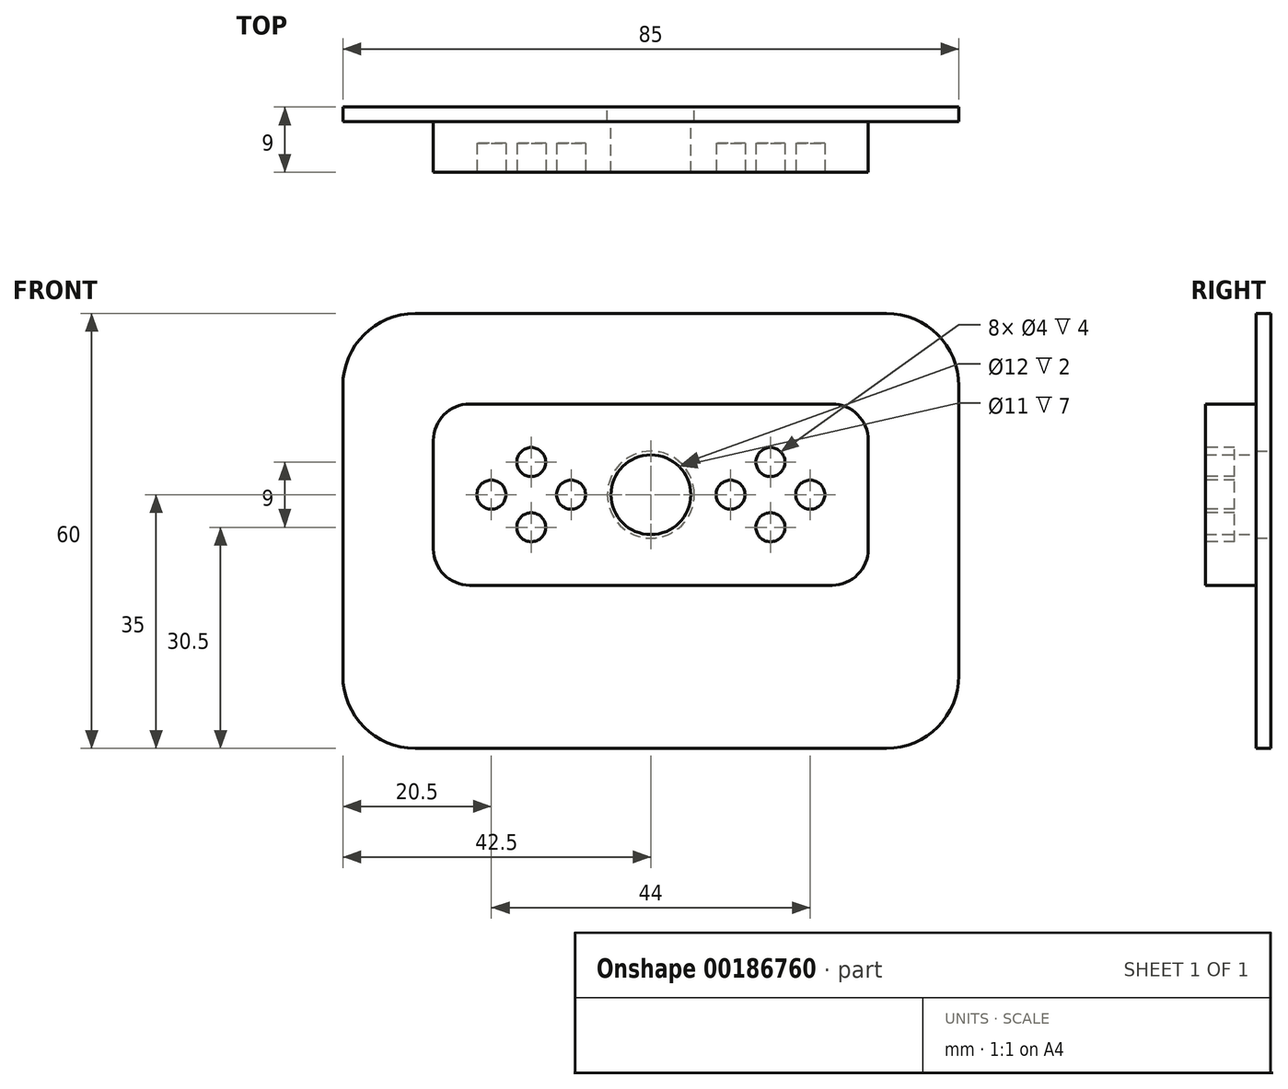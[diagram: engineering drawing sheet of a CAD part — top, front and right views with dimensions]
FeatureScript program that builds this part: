
annotation { "Feature Type Name" : "Feature", "Feature Type Description" : "" }
export const myFeature = defineFeature(function(context is Context, id is Id, definition is map)
    precondition{}
    {
        {
            var Q0;
            Q0=qCreatedBy(makeId("Front.planeOp"),FACE);
            var sketch = newSketch(context, id + "F0", { "sketchPlane" : qUnion([Q0])});
            skLineSegment(sketch, "E0.bottom", {"start": v(42.5, -35) * mm, "end": v(-42.5, -35) * mm});
            skLineSegment(sketch, "E0.top", {"start": v(42.5, 25) * mm, "end": v(-42.5, 25) * mm});
            skLineSegment(sketch, "E0.left", {"start": v(42.5, -35) * mm, "end": v(42.5, 25) * mm});
            skLineSegment(sketch, "E0.right", {"start": v(-42.5, -35) * mm, "end": v(-42.5, 25) * mm});
            skCircle(sketch, "E1", {"center": v(0, 0) * mm, "radius": 6 * mm});
            skSolve(sketch);
        }
        {
            var Q0;
            Q0 = qSketchRegion(id + "F0", true);
            extrude(context, id + "F1", {"entities" : qUnion([Q0]), "depth" : 2 * mm});
        }
        {
            var Q0;
            Q0=makeQuery(id+"F1.opExtrude","CAP_FACE",FACE,{"disambiguationData":[OSD([sQuery(id+"F0.wireOp",EDGE,"E0.bottom"),sQuery(id+"F0.wireOp",EDGE,"E0.top"),sQuery(id+"F0.wireOp",EDGE,"E0.left"),sQuery(id+"F0.wireOp",EDGE,"E0.right"),sQuery(id+"F0.wireOp",EDGE,"E1")])],"isStart":false});
            var sketch = newSketch(context, id + "F2", { "sketchPlane" : qUnion([Q0])});
            skLineSegment(sketch, "E2.bottom", {"start": v(-30, 12.5) * mm, "end": v(30, 12.5) * mm});
            skLineSegment(sketch, "E2.top", {"start": v(-30, -12.5) * mm, "end": v(30, -12.5) * mm});
            skLineSegment(sketch, "E2.left", {"start": v(-30, 12.5) * mm, "end": v(-30, -12.5) * mm});
            skLineSegment(sketch, "E2.right", {"start": v(30, 12.5) * mm, "end": v(30, -12.5) * mm});
            skPoint(sketch, "E2.middle", {"position": v(0, 0) * mm});
            skCircle(sketch, "E3", {"center": v(0, 0) * mm, "radius": 5.5 * mm});
            skSolve(sketch);
        }
        {
            var Q0;
            Q0 = qSketchRegion(id + "F2", true);
            extrude(context, id + "F3", {"entities" : qUnion([Q0]), "operationType" : NewBodyOperationType.ADD, "depth" : 7 * mm});
        }
        {
            var Q0;
            Q0=makeQuery(id+"F3.opExtrude","SWEPT_EDGE",EDGE,{"disambiguationData":[OSD([sQuery(id+"F2.wireOp",EDGE,"E2.bottom"),sQuery(id+"F2.wireOp",EDGE,"E2.right")])]});
            var Q1;
            Q1=makeQuery(id+"F3.opExtrude","SWEPT_EDGE",EDGE,{"disambiguationData":[OSD([sQuery(id+"F2.wireOp",EDGE,"E2.top"),sQuery(id+"F2.wireOp",EDGE,"E2.right")])]});
            var Q2;
            Q2=makeQuery(id+"F3.opExtrude","SWEPT_EDGE",EDGE,{"disambiguationData":[OSD([sQuery(id+"F2.wireOp",EDGE,"E2.top"),sQuery(id+"F2.wireOp",EDGE,"E2.left")])]});
            var Q3;
            Q3=makeQuery(id+"F3.opExtrude","SWEPT_EDGE",EDGE,{"disambiguationData":[OSD([sQuery(id+"F2.wireOp",EDGE,"E2.bottom"),sQuery(id+"F2.wireOp",EDGE,"E2.left")])]});
            fillet(context, id + "F4", {"entities" : qUnion([Q0, Q1, Q2, Q3]), "radius" : 5 * mm, "tangentPropagation" : true, "allowEdgeOverflow" : false});
        }
        {
            var Q0;
            Q0=makeQuery(id+"F1.opExtrude","SWEPT_EDGE",EDGE,{"disambiguationData":[OSD([sQuery(id+"F0.wireOp",EDGE,"E0.top"),sQuery(id+"F0.wireOp",EDGE,"E0.left")])]});
            var Q1;
            Q1=makeQuery(id+"F1.opExtrude","SWEPT_EDGE",EDGE,{"disambiguationData":[OSD([sQuery(id+"F0.wireOp",EDGE,"E0.bottom"),sQuery(id+"F0.wireOp",EDGE,"E0.left")])]});
            var Q2;
            Q2=makeQuery(id+"F1.opExtrude","SWEPT_EDGE",EDGE,{"disambiguationData":[OSD([sQuery(id+"F0.wireOp",EDGE,"E0.bottom"),sQuery(id+"F0.wireOp",EDGE,"E0.right")])]});
            var Q3;
            Q3=makeQuery(id+"F1.opExtrude","SWEPT_EDGE",EDGE,{"disambiguationData":[OSD([sQuery(id+"F0.wireOp",EDGE,"E0.top"),sQuery(id+"F0.wireOp",EDGE,"E0.right")])]});
            fillet(context, id + "F5", {"entities" : qUnion([Q0, Q1, Q2, Q3]), "radius" : 10 * mm, "tangentPropagation" : true, "allowEdgeOverflow" : false});
        }
        {
            var Q0;
            Q0=makeQuery(id+"F3.opExtrude","CAP_FACE",FACE,{"disambiguationData":[OSD([sQuery(id+"F2.wireOp",EDGE,"E2.bottom"),sQuery(id+"F2.wireOp",EDGE,"E2.top"),sQuery(id+"F2.wireOp",EDGE,"E2.left"),sQuery(id+"F2.wireOp",EDGE,"E2.right"),sQuery(id+"F2.wireOp",EDGE,"E3")])],"isStart":false});
            var sketch = newSketch(context, id + "F6", { "sketchPlane" : qUnion([Q0])});
            skCircle(sketch, "E4", {"center": v(-11, 0) * mm, "radius": 2 * mm});
            skCircle(sketch, "E5", {"center": v(-22, 0) * mm, "radius": 2 * mm});
            skCircle(sketch, "E6", {"center": v(11, 0) * mm, "radius": 2 * mm});
            skCircle(sketch, "E7", {"center": v(22, 0) * mm, "radius": 2 * mm});
            skCircle(sketch, "E8", {"center": v(-16.5, -4.5) * mm, "radius": 2 * mm});
            skCircle(sketch, "E9", {"center": v(16.5, -4.5) * mm, "radius": 2 * mm});
            skCircle(sketch, "E10", {"center": v(16.5, 4.5) * mm, "radius": 2 * mm});
            skCircle(sketch, "E11", {"center": v(-16.5, 4.5) * mm, "radius": 2 * mm});
            skSolve(sketch);
        }
        {
            var Q0;
            Q0 = qSketchRegion(id + "F6", true);
            extrude(context, id + "F7", {"entities" : qUnion([Q0]), "operationType" : NewBodyOperationType.REMOVE, "oppositeDirection" : true, "depth" : 4 * mm});
        }
    });
